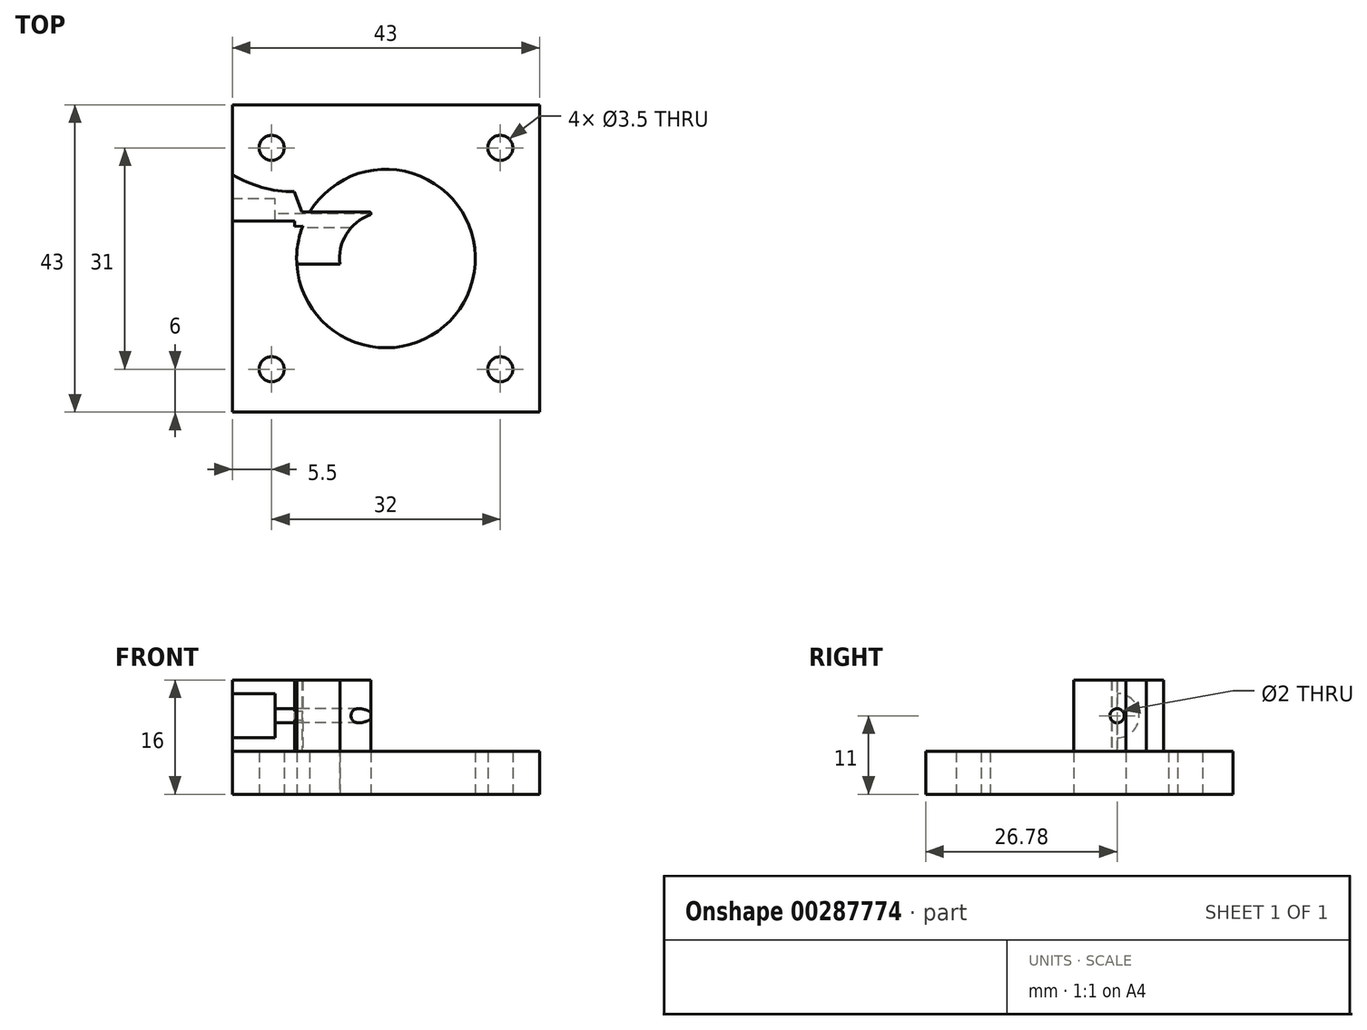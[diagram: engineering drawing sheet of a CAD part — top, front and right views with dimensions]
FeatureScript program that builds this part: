
annotation { "Feature Type Name" : "Feature", "Feature Type Description" : "" }
export const myFeature = defineFeature(function(context is Context, id is Id, definition is map)
    precondition{}
    {
        {
            var Q0;
            Q0=qCreatedBy(makeId("Top.planeOp"),FACE);
            var sketch = newSketch(context, id + "F0", { "sketchPlane" : qUnion([Q0])});
            skLineSegment(sketch, "E0.bottom", {"start": v(21.5, 21.5) * mm, "end": v(-21.5, 21.5) * mm});
            skLineSegment(sketch, "E0.top", {"start": v(21.5, -21.5) * mm, "end": v(-21.5, -21.5) * mm});
            skLineSegment(sketch, "E0.left", {"start": v(21.5, 21.5) * mm, "end": v(21.5, -21.5) * mm});
            skLineSegment(sketch, "E0.right", {"start": v(-21.5, 21.5) * mm, "end": v(-21.5, -21.5) * mm});
            skPoint(sketch, "E0.middle", {"position": v(0, 0) * mm});
            skLineSegment(sketch, "E1.bottom", {"start": v(16, 15.5) * mm, "end": v(-16, 15.5) * mm});
            skCircle(sketch, "E2", {"center": v(-16, -15.5) * mm, "radius": 1.75 * mm});
            skCircle(sketch, "E3", {"center": v(16, -15.5) * mm, "radius": 1.75 * mm});
            skCircle(sketch, "E4", {"center": v(0, 0) * mm, "radius": 12.5 * mm});
            skCircle(sketch, "E5", {"center": v(-16, 15.5) * mm, "radius": 1.75 * mm});
            skCircle(sketch, "E6", {"center": v(16, 15.5) * mm, "radius": 1.75 * mm});
            skSolve(sketch);
        }
        {
            var Q0;
            Q0=makeQuery(id+"F0.imprint","IMPRINT",FACE,{"disambiguationData":[TD([[makeQuery(id+"F0.imprint","IMPRINT",EDGE,{"derivedFrom":sQuery(id+"F0.wireOp",EDGE,"E0.bottom")}),1.0]])]});
            extrude(context, id + "F1", {"entities" : qUnion([Q0]), "depth" : 6 * mm});
        }
        {
            var Q0;
            Q0=makeQuery(id+"F1.opExtrude","CAP_FACE",FACE,{"disambiguationData":[OSD([sQuery(id+"F0.wireOp",EDGE,"E0.bottom"),sQuery(id+"F0.wireOp",EDGE,"E0.top"),sQuery(id+"F0.wireOp",EDGE,"E0.left"),sQuery(id+"F0.wireOp",EDGE,"E0.right"),sQuery(id+"F0.wireOp",EDGE,"E2"),sQuery(id+"F0.wireOp",EDGE,"E3"),sQuery(id+"F0.wireOp",EDGE,"E4"),sQuery(id+"F0.wireOp",EDGE,"E5"),sQuery(id+"F0.wireOp",EDGE,"E6")])],"isStart":false});
            var sketch = newSketch(context, id + "F2", { "sketchPlane" : qUnion([Q0])});
            skCircle(sketch, "E7", {"center": v(0, 0) * mm, "radius": 5.28 * mm});
            skLineSegment(sketch, "E8", {"start": v(0, 5.28) * mm, "end": v(21.5, 5.28) * mm});
            skLineSegment(sketch, "E9", {"start": v(0, 5.28) * mm, "end": v(-21.5, 5.28) * mm});
            skLineSegment(sketch, "E10.bottom", {"start": v(-21.5, 5.28) * mm, "end": v(-4.18, 5.28) * mm});
            skLineSegment(sketch, "E10.left", {"start": v(-21.5, 5.28) * mm, "end": v(-21.5, 11.78) * mm});
            skArc(sketch, "E11", {"start": v(-4.18, 11.78) * mm, "mid": v(-8.4, 9.23) * mm, "end": v(-11.33, 5.28) * mm});
            skLineSegment(sketch, "E12.bottom", {"start": v(-21.5, 5.28) * mm, "end": v(-11.34, 5.28) * mm});
            skLineSegment(sketch, "E12.top", {"start": v(-21.5, -4.72) * mm, "end": v(-11.34, -4.72) * mm});
            skLineSegment(sketch, "E12.left", {"start": v(-21.5, 5.28) * mm, "end": v(-21.5, -4.72) * mm});
            skArc(sketch, "E13", {"start": v(-11.33, 5.28) * mm, "mid": v(-12.46, 0.3) * mm, "end": v(-11.57, -4.72) * mm});
            skArc(sketch, "E14", {"start": v(-21.5, 11.78) * mm, "mid": v(-12.84, 9.35) * mm, "end": v(-4.18, 11.78) * mm});
            skLineSegment(sketch, "E15.bottom", {"start": v(21.5, 5.28) * mm, "end": v(11.5, 5.28) * mm});
            skLineSegment(sketch, "E15.top", {"start": v(21.5, 9.36) * mm, "end": v(11.5, 9.36) * mm});
            skLineSegment(sketch, "E15.left", {"start": v(21.5, 5.28) * mm, "end": v(21.5, 9.36) * mm});
            skLineSegment(sketch, "E15.right", {"start": v(11.5, 5.28) * mm, "end": v(11.5, 9.36) * mm});
            skLineSegment(sketch, "E16.bottom", {"start": v(21.5, 5.28) * mm, "end": v(12.28, 5.28) * mm});
            skLineSegment(sketch, "E16.top", {"start": v(21.5, 2.31) * mm, "end": v(12.28, 2.31) * mm});
            skLineSegment(sketch, "E16.left", {"start": v(21.5, 5.28) * mm, "end": v(21.5, 2.31) * mm});
            skLineSegment(sketch, "E16.right", {"start": v(12.28, 5.28) * mm, "end": v(12.28, 2.31) * mm});
            skArc(sketch, "E17", {"start": v(12.28, 2.31) * mm, "mid": v(12, 3.82) * mm, "end": v(11.5, 5.28) * mm});
            skLineSegment(sketch, "E18", {"start": v(-12.84, 9.35) * mm, "end": v(-11.33, 5.28) * mm});
            skSolve(sketch);
        }
        {
            var Q0;
            {var subQ1=sQuery(id+"F2.wireOp",EDGE,"E10.left");Q0=makeQuery(id+"F2.imprint","IMPRINT",FACE,{"disambiguationData":[TD([[makeQuery(id+"F2.imprint","IMPRINT",EDGE,{"derivedFrom":subQ1}),1.0]])]});}
            var Q1;
            {var subQ5=sQuery(id+"F2.wireOp",EDGE,"E12.bottom");Q1=makeQuery(id+"F2.imprint","IMPRINT",FACE,{"disambiguationData":[TD([[makeQuery(id+"F2.imprint","IMPRINT",EDGE,{"derivedFrom":subQ5}),1.0]])]});}
            var Q2;
            Q2=makeQuery(id+"F2.imprint","IMPRINT",FACE,{"disambiguationData":[TD([[makeQuery(id+"F2.imprint","IMPRINT",EDGE,{"derivedFrom":sQuery(id+"F2.wireOp",EDGE,"E15.bottom")}),-1.0]])]});
            var Q3;
            Q3=makeQuery(id+"F2.imprint","IMPRINT",FACE,{"disambiguationData":[TD([[makeQuery(id+"F2.imprint","IMPRINT",EDGE,{"derivedFrom":sQuery(id+"F2.wireOp",EDGE,"E16.bottom")}),1.0]])]});
            var Q4;
            Q4=makeQuery(id+"F2.imprint","IMPRINT",FACE,{"disambiguationData":[TD([[makeQuery(id+"F2.imprint","IMPRINT",EDGE,{"derivedFrom":sQuery(id+"F2.wireOp",EDGE,"E15.bottom")}),1.0]])]});
            extrude(context, id + "F3", {"entities" : qUnion([Q0, Q1, Q2, Q3, Q4]), "operationType" : NewBodyOperationType.ADD, "depth" : 10 * mm});
        }
        {
            var Q0;
            Q0=makeQuery(id+"F3.boolean.opBoolean","MERGE",FACE,{"derivedFrom":[makeQuery(id+"F1.opExtrude","SWEPT_FACE",FACE,{"disambiguationData":[OSD([sQuery(id+"F0.wireOp",EDGE,"E0.right")])]}),makeQuery(id+"F3.opExtrude","SWEPT_FACE",FACE,{"disambiguationData":[OSD([sQuery(id+"F2.wireOp",EDGE,"E10.left"),sQuery(id+"F2.wireOp",EDGE,"E12.left")])]})]});
            var sketch = newSketch(context, id + "F4", { "sketchPlane" : qUnion([Q0])});
            skLineSegment(sketch, "E19", {"start": v(0, 0) * mm, "end": v(-5.28, 0) * mm});
            skLineSegment(sketch, "E20", {"start": v(-11.78, 11) * mm, "end": v(4.72, 11) * mm});
            skLineSegment(sketch, "E21", {"start": v(-5.28, 0) * mm, "end": v(-5.28, 11) * mm});
            skCircle(sketch, "E22", {"center": v(-5.28, 11) * mm, "radius": 3.1 * mm});
            skSolve(sketch);
        }
        {
            var Q0;
            {var subQ0=sQuery(id+"F4.wireOp",EDGE,"E21");var subQ1=sQuery(id+"F4.wireOp",EDGE,"E20");var subQ2=makeQuery(id+"F4.imprint","INTERSECT",VERTEX,{"derivedFrom":[subQ1,subQ0]});Q0=makeQuery(id+"F4.imprint","IMPRINT",FACE,{"disambiguationData":[TD([[makeQuery(id+"F4.imprint","IMPRINT",EDGE,{"disambiguationData":[TD([[subQ2,-1.0]])],"derivedFrom":subQ1}),-1.0]])]});}
            var Q1;
            {var subQ0=sQuery(id+"F4.wireOp",EDGE,"E21");var subQ1=sQuery(id+"F4.wireOp",EDGE,"E20");var subQ2=makeQuery(id+"F4.imprint","INTERSECT",VERTEX,{"derivedFrom":[subQ1,subQ0]});Q1=makeQuery(id+"F4.imprint","IMPRINT",FACE,{"disambiguationData":[TD([[makeQuery(id+"F4.imprint","IMPRINT",EDGE,{"disambiguationData":[TD([[subQ2,1.0]])],"derivedFrom":subQ1}),-1.0]])]});}
            var Q2;
            {var subQ0=sQuery(id+"F4.wireOp",EDGE,"E20");var subQ1=makeQuery(id+"F4.imprint","INTERSECT",VERTEX,{"derivedFrom":[subQ0,sQuery(id+"F4.wireOp",EDGE,"E21")]});Q2=makeQuery(id+"F4.imprint","IMPRINT",FACE,{"disambiguationData":[TD([[makeQuery(id+"F4.imprint","IMPRINT",EDGE,{"disambiguationData":[TD([[subQ1,1.0]])],"derivedFrom":subQ0}),1.0]])]});}
            extrude(context, id + "F5", {"entities" : qUnion([Q0, Q1, Q2]), "operationType" : NewBodyOperationType.REMOVE, "oppositeDirection" : true, "depth" : 6 * mm});
        }
        {
            var Q0;
            Q0=makeQuery(id+"F5.boolean.opBoolean","COPY",FACE,{"derivedFrom":makeQuery(id+"F5.opExtrude","CAP_FACE",FACE,{"disambiguationData":[OSD([sQuery(id+"F4.wireOp",EDGE,"E22")])],"isStart":false})});
            var sketch = newSketch(context, id + "F6", { "sketchPlane" : qUnion([Q0])});
            skCircle(sketch, "E23", {"center": v(-5.28, 11) * mm, "radius": 1 * mm});
            skSolve(sketch);
        }
        {
            var Q0;
            Q0=qCreatedBy(makeId("Top.planeOp"),FACE);
            var sketch = newSketch(context, id + "F7", { "sketchPlane" : qUnion([Q0])});
            skCircle(sketch, "E24", {"center": v(0, 0) * mm, "radius": 5.28 * mm});
            skCircle(sketch, "E25", {"center": v(0, 0) * mm, "radius": 12.5 * mm});
            skCircle(sketch, "E26", {"center": v(0, 0) * mm, "radius": 6.5 * mm});
            skLineSegment(sketch, "E27", {"start": v(-12.47, -0.8) * mm, "end": v(-5.22, -0.8) * mm});
            skLineSegment(sketch, "E28", {"start": v(0, 6.5) * mm, "end": v(-10.68, 6.5) * mm});
            skLineSegment(sketch, "E29", {"start": v(-10.68, 6.5) * mm, "end": v(-12.87, 6.5) * mm});
            skLineSegment(sketch, "E30", {"start": v(-12.87, 6.5) * mm, "end": v(-12.76, 4.5) * mm});
            skLineSegment(sketch, "E31", {"start": v(-12.76, 4.5) * mm, "end": v(-9.9, 4.66) * mm});
            skLineSegment(sketch, "E32", {"start": v(-9.9, 4.66) * mm, "end": v(-9.9, 6.5) * mm});
            skSolve(sketch);
        }
        {
            var Q0;
            {var subQ0=sQuery(id+"F7.wireOp",EDGE,"E28");Q0=makeQuery(id+"F7.imprint","IMPRINT",FACE,{"disambiguationData":[TD([[makeQuery(id+"F7.imprint","IMPRINT",EDGE,{"derivedFrom":subQ0}),1.0]])]});}
            var Q1;
            {var subQ3=sQuery(id+"F7.wireOp",EDGE,"E32");Q1=makeQuery(id+"F7.imprint","IMPRINT",FACE,{"disambiguationData":[TD([[makeQuery(id+"F7.imprint","IMPRINT",EDGE,{"derivedFrom":subQ3}),-1.0]])]});}
            var Q2;
            {var subQ0=sQuery(id+"F7.wireOp",EDGE,"E29");Q2=makeQuery(id+"F7.imprint","IMPRINT",FACE,{"disambiguationData":[TD([[makeQuery(id+"F7.imprint","IMPRINT",EDGE,{"derivedFrom":subQ0}),1.0]])]});}
            extrude(context, id + "F8", {"entities" : qUnion([Q0, Q1, Q2]), "operationType" : NewBodyOperationType.ADD, "depth" : 16 * mm});
        }
        {
            var Q0;
            Q0=makeQuery(id+"F8.opExtrude","SWEPT_EDGE",EDGE,{"disambiguationData":[OSD([sQuery(id+"F7.wireOp",EDGE,"E26"),sQuery(id+"F7.wireOp",EDGE,"E28")])]});
            fillet(context, id + "F9", {"entities" : qUnion([Q0]), "radius" : .2 * mm, "tangentPropagation" : true, "allowEdgeOverflow" : false});
        }
        {
            var Q0;
            Q0=makeQuery(id+"F6.imprint","IMPRINT",FACE,{"disambiguationData":[TD([[makeQuery(id+"F6.imprint","IMPRINT",EDGE,{"derivedFrom":sQuery(id+"F6.wireOp",EDGE,"E23")}),1.0]])]});
            extrude(context, id + "F10", {"entities" : qUnion([Q0]), "operationType" : NewBodyOperationType.REMOVE, "oppositeDirection" : true, "depth" : 70 * mm});
        }
    });
